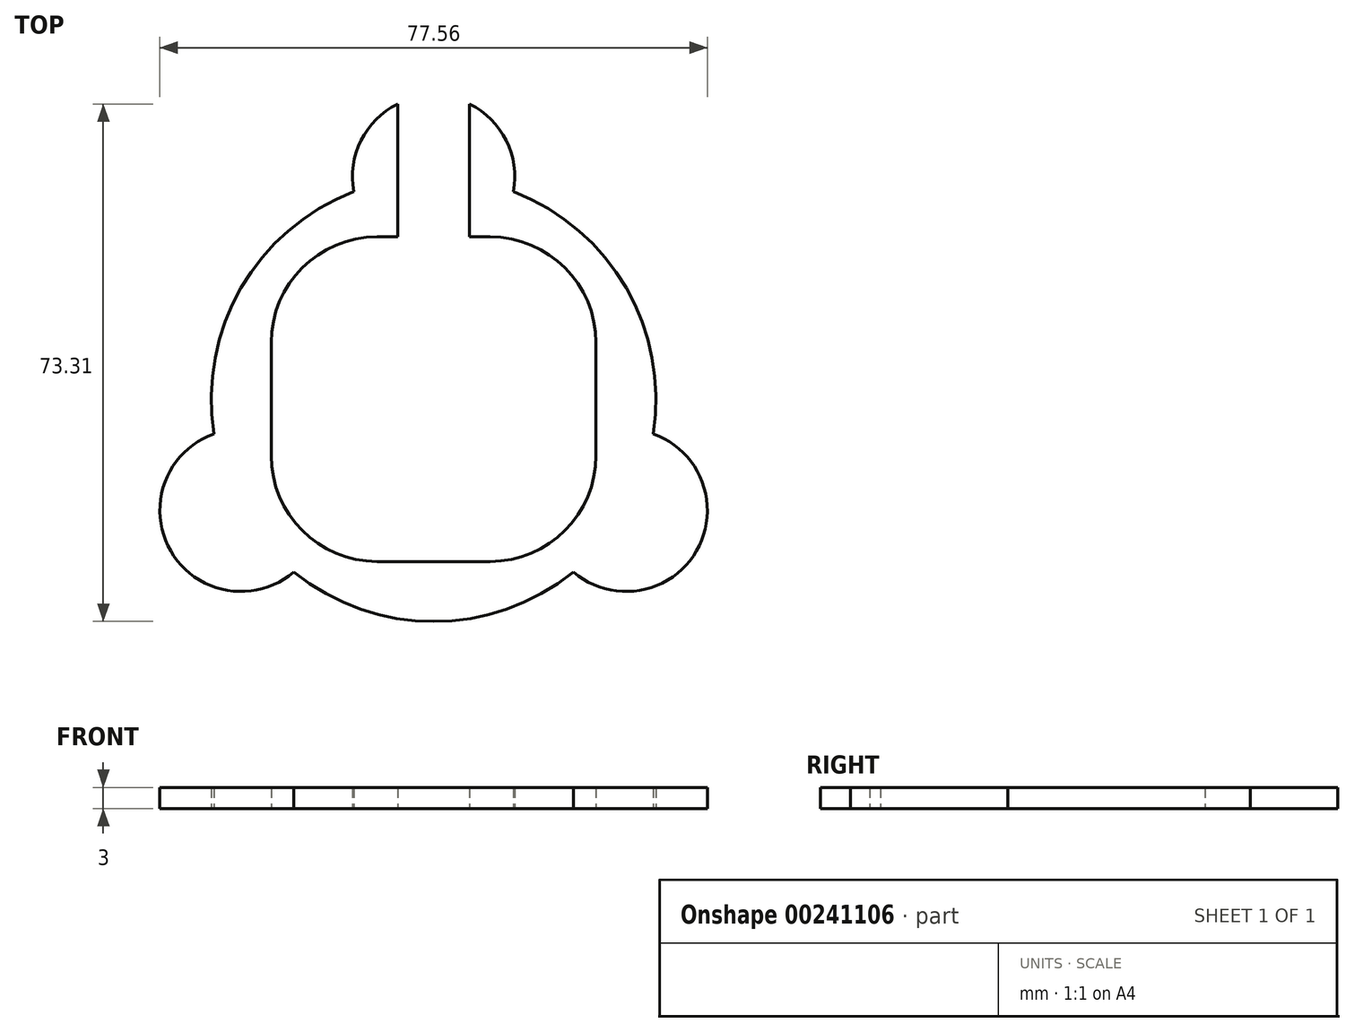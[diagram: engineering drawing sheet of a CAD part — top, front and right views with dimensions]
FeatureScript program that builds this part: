
annotation { "Feature Type Name" : "Feature", "Feature Type Description" : "" }
export const myFeature = defineFeature(function(context is Context, id is Id, definition is map)
    precondition{}
    {
        {
            var Q0;
            Q0=qCreatedBy(makeId("Top.planeOp"),FACE);
            var sketch = newSketch(context, id + "F0", { "sketchPlane" : qUnion([Q0])});
            skPoint(sketch, "E0.center", {"position": v(0, 0) * mm});
            skCircle(sketch, "E1", {"center": v(0, 31.5) * mm, "radius": 11.5 * mm});
            skCircle(sketch, "E2.1.0", {"center": v(-27.28, -15.75) * mm, "radius": 11.5 * mm});
            skCircle(sketch, "E2.2.0", {"center": v(27.28, -15.75) * mm, "radius": 11.5 * mm});
            skCircle(sketch, "E3", {"center": v(0, 0) * mm, "radius": 31.5 * mm});
            skSolve(sketch);
        }
        {
            var Q0;
            Q0=qCreatedBy(makeId("Top.planeOp"),FACE);
            var sketch = newSketch(context, id + "F1", { "sketchPlane" : qUnion([Q0])});
            skLineSegment(sketch, "E4.bottom", {"start": v(5.1, 16.8) * mm, "end": v(-5.1, 16.8) * mm});
            skLineSegment(sketch, "E4.top", {"start": v(5.1, 46.27) * mm, "end": v(-5.1, 46.27) * mm});
            skLineSegment(sketch, "E4.left", {"start": v(5.1, 16.8) * mm, "end": v(5.1, 46.27) * mm});
            skLineSegment(sketch, "E4.right", {"start": v(-5.1, 16.8) * mm, "end": v(-5.1, 46.27) * mm});
            skPoint(sketch, "E4.middle", {"position": v(0, 31.54) * mm});
            skLineSegment(sketch, "E5.bottom", {"start": v(8, -23) * mm, "end": v(-8, -23) * mm});
            skLineSegment(sketch, "E5.top", {"start": v(8, 23) * mm, "end": v(-8, 23) * mm});
            skLineSegment(sketch, "E5.left", {"start": v(23, -8) * mm, "end": v(23, 8) * mm});
            skLineSegment(sketch, "E5.right", {"start": v(-23, -8) * mm, "end": v(-23, 8) * mm});
            skPoint(sketch, "E5.middle", {"position": v(0, 0) * mm});
            skPoint(sketch, "E6.visualSharp", {"position": v(23, 23) * mm});
            skArc(sketch, "E6.filletArc", {"start": v(23, 8) * mm, "mid": v(18.6, 18.6) * mm, "end": v(8, 23) * mm});
            skPoint(sketch, "E7.visualSharp", {"position": v(-23, 23) * mm});
            skArc(sketch, "E7.filletArc", {"start": v(-8, 23) * mm, "mid": v(-18.6, 18.6) * mm, "end": v(-23, 8) * mm});
            skPoint(sketch, "E8.visualSharp", {"position": v(-23, -23) * mm});
            skArc(sketch, "E8.filletArc", {"start": v(-23, -8) * mm, "mid": v(-18.6, -18.6) * mm, "end": v(-8, -23) * mm});
            skPoint(sketch, "E9.visualSharp", {"position": v(23, -23) * mm});
            skArc(sketch, "E9.filletArc", {"start": v(8, -23) * mm, "mid": v(18.6, -18.6) * mm, "end": v(23, -8) * mm});
            skSolve(sketch);
        }
        {
            var Q0;
            Q0 = qSketchRegion(id + "F0", true);
            extrude(context, id + "F2", {"entities" : qUnion([Q0]), "depth" : 3 * mm});
        }
        {
            var Q0;
            Q0 = qSketchRegion(id + "F1", true);
            extrude(context, id + "F3", {"entities" : qUnion([Q0]), "operationType" : NewBodyOperationType.REMOVE, "depth" : 3 * mm});
        }
    });
